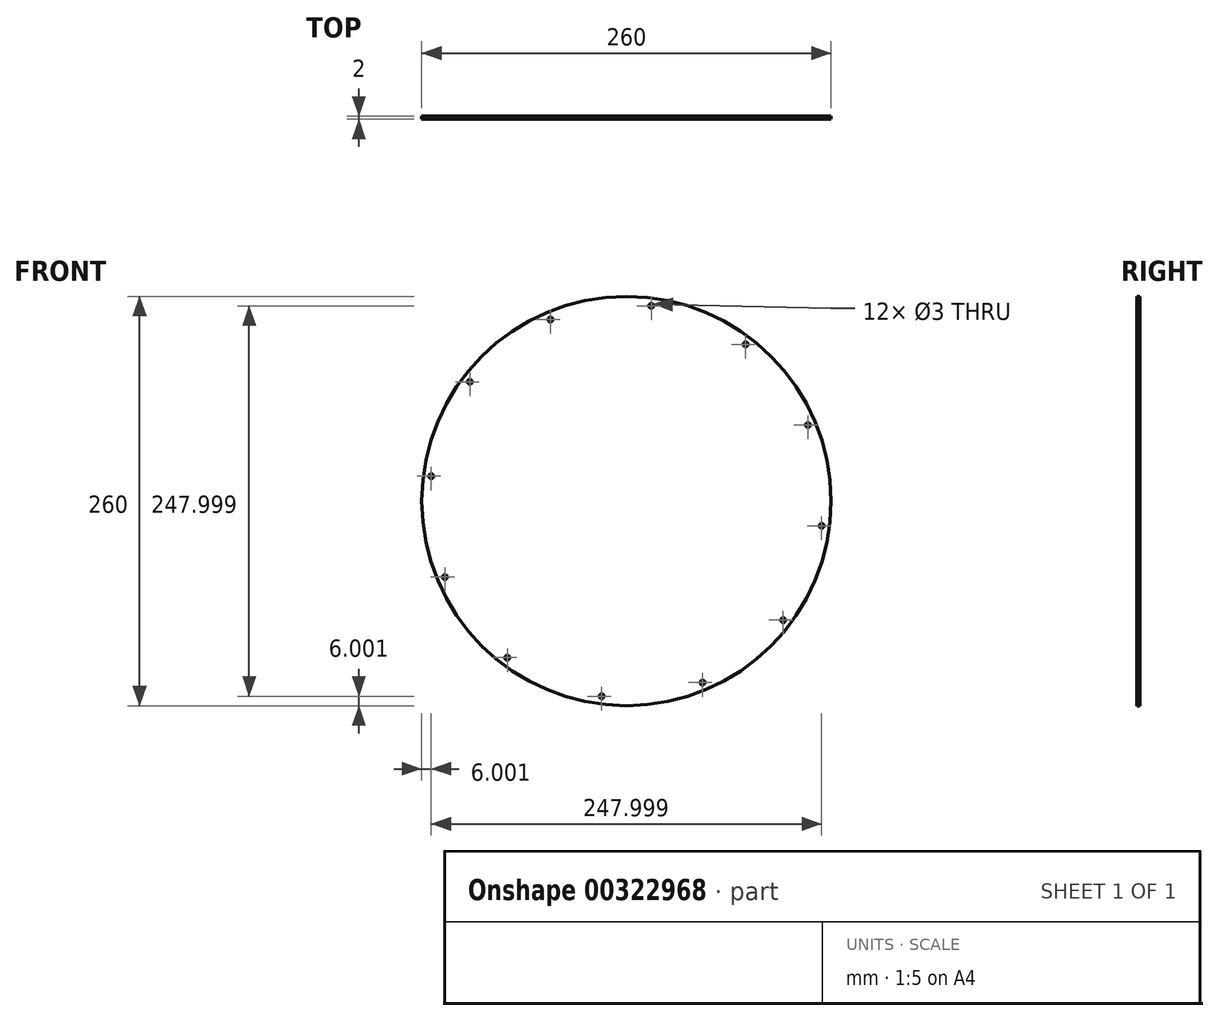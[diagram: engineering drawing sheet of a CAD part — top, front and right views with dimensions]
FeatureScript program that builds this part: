
annotation { "Feature Type Name" : "Feature", "Feature Type Description" : "" }
export const myFeature = defineFeature(function(context is Context, id is Id, definition is map)
    precondition{}
    {
        {
            var Q0;
            Q0=qCreatedBy(makeId("Front.planeOp"),FACE);
            var sketch = newSketch(context, id + "F0", { "sketchPlane" : qUnion([Q0])});
            skCircle(sketch, "E0", {"center": v(0, 0) * mm, "radius": 130 * mm});
            skCircle(sketch, "E1", {"center": v(0, 0) * mm, "radius": 125 * mm, "construction": true});
            skLineSegment(sketch, "E2.0", {"start": v(124, -15.78) * mm, "end": v(99.5, -75.67) * mm, "construction": true});
            skLineSegment(sketch, "E2.1", {"start": v(99.5, -75.67) * mm, "end": v(48.33, -115.28) * mm, "construction": true});
            skLineSegment(sketch, "E2.2", {"start": v(48.33, -115.28) * mm, "end": v(-15.78, -124) * mm, "construction": true});
            skLineSegment(sketch, "E2.3", {"start": v(-15.78, -124) * mm, "end": v(-75.67, -99.5) * mm, "construction": true});
            skLineSegment(sketch, "E2.4", {"start": v(-75.67, -99.5) * mm, "end": v(-115.28, -48.33) * mm, "construction": true});
            skLineSegment(sketch, "E2.5", {"start": v(-115.28, -48.33) * mm, "end": v(-124, 15.78) * mm, "construction": true});
            skLineSegment(sketch, "E2.6", {"start": v(-124, 15.78) * mm, "end": v(-99.5, 75.67) * mm, "construction": true});
            skLineSegment(sketch, "E2.7", {"start": v(-99.5, 75.67) * mm, "end": v(-48.33, 115.28) * mm, "construction": true});
            skLineSegment(sketch, "E2.8", {"start": v(-48.33, 115.28) * mm, "end": v(15.78, 124) * mm, "construction": true});
            skLineSegment(sketch, "E2.9", {"start": v(15.78, 124) * mm, "end": v(75.67, 99.5) * mm, "construction": true});
            skLineSegment(sketch, "E2.10", {"start": v(75.67, 99.5) * mm, "end": v(115.28, 48.33) * mm, "construction": true});
            skLineSegment(sketch, "E2.11", {"start": v(115.28, 48.33) * mm, "end": v(124, -15.78) * mm, "construction": true});
            skCircle(sketch, "E3", {"center": v(-115.28, -48.33) * mm, "radius": 1.5 * mm});
            skCircle(sketch, "E4", {"center": v(-124, 15.78) * mm, "radius": 1.5 * mm});
            skCircle(sketch, "E5", {"center": v(-99.5, 75.67) * mm, "radius": 1.5 * mm});
            skCircle(sketch, "E6", {"center": v(-75.67, -99.5) * mm, "radius": 1.5 * mm});
            skCircle(sketch, "E7", {"center": v(-15.78, -124) * mm, "radius": 1.5 * mm});
            skCircle(sketch, "E8", {"center": v(48.33, -115.28) * mm, "radius": 1.5 * mm});
            skCircle(sketch, "E9", {"center": v(99.5, -75.67) * mm, "radius": 1.5 * mm});
            skCircle(sketch, "E10", {"center": v(124, -15.78) * mm, "radius": 1.5 * mm});
            skCircle(sketch, "E11", {"center": v(115.28, 48.33) * mm, "radius": 1.5 * mm});
            skCircle(sketch, "E12", {"center": v(75.67, 99.5) * mm, "radius": 1.5 * mm});
            skCircle(sketch, "E13", {"center": v(15.78, 124) * mm, "radius": 1.5 * mm});
            skCircle(sketch, "E14", {"center": v(-48.33, 115.28) * mm, "radius": 1.5 * mm});
            skSolve(sketch);
        }
        {
            var Q0;
            Q0=makeQuery(id+"F0.imprint","IMPRINT",FACE,{"disambiguationData":[TD([[makeQuery(id+"F0.imprint","IMPRINT",EDGE,{"derivedFrom":sQuery(id+"F0.wireOp",EDGE,"E0")}),1.0]])]});
            extrude(context, id + "F1", {"entities" : qUnion([Q0]), "depth" : 2 * mm});
        }
    });
